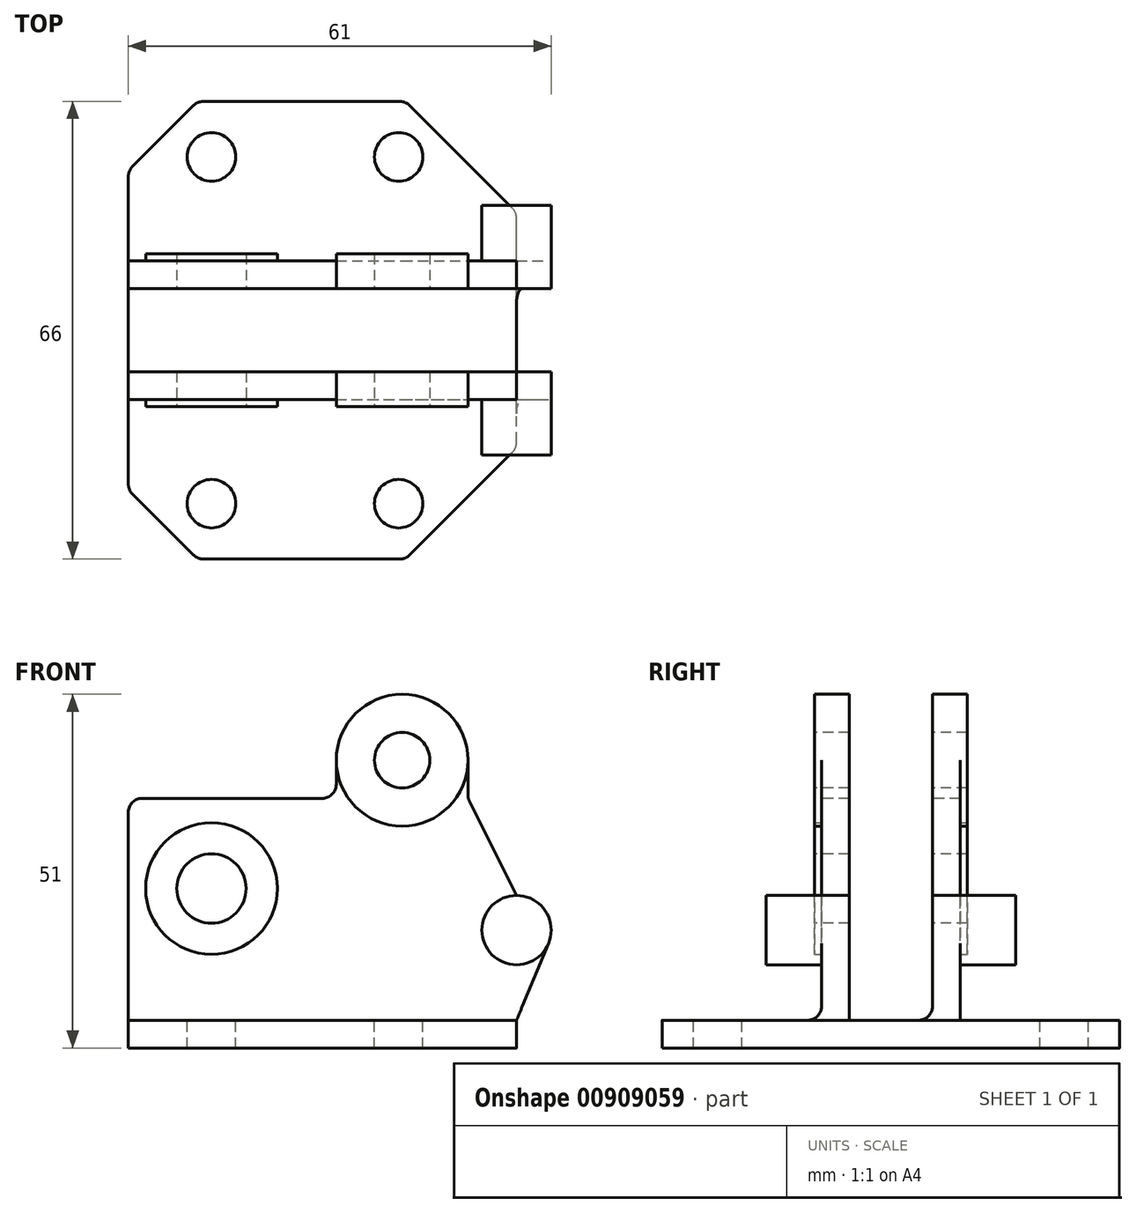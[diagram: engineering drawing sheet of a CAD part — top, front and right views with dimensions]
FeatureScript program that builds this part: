
annotation { "Feature Type Name" : "Feature", "Feature Type Description" : "" }
export const myFeature = defineFeature(function(context is Context, id is Id, definition is map)
    precondition{}
    {
        {
            var Q0;
            Q0=qCreatedBy(makeId("Top.planeOp"),FACE);
            var sketch = newSketch(context, id + "F0", { "sketchPlane" : qUnion([Q0])});
            skLineSegment(sketch, "E0.bottom", {"start": v(0, 0) * mm, "end": v(56, 0) * mm});
            skLineSegment(sketch, "E0.top", {"start": v(0, 66) * mm, "end": v(56, 66) * mm});
            skLineSegment(sketch, "E0.left", {"start": v(0, 0) * mm, "end": v(0, 66) * mm});
            skLineSegment(sketch, "E0.right", {"start": v(56, 0) * mm, "end": v(56, 66) * mm});
            skSolve(sketch);
        }
        {
            var Q0;
            Q0=makeQuery(id+"F0.imprint","IMPRINT",FACE,{"disambiguationData":[TD([[makeQuery(id+"F0.imprint","IMPRINT",EDGE,{"derivedFrom":sQuery(id+"F0.wireOp",EDGE,"E0.bottom")}),1.0]])]});
            extrude(context, id + "F1", {"entities" : qUnion([Q0]), "depth" : 4 * mm, "offsetDistance" : 25 * mm});
        }
        {
            var Q0;
            Q0=makeQuery(id+"F1.opExtrude","CAP_FACE",FACE,{"disambiguationData":[OSD([sQuery(id+"F0.wireOp",EDGE,"E0.bottom"),sQuery(id+"F0.wireOp",EDGE,"E0.top"),sQuery(id+"F0.wireOp",EDGE,"E0.left"),sQuery(id+"F0.wireOp",EDGE,"E0.right")])],"isStart":false});
            var sketch = newSketch(context, id + "F2", { "sketchPlane" : qUnion([Q0])});
            skPoint(sketch, "E1", {"position": v(12, 58) * mm});
            skPoint(sketch, "E2.0.1.0", {"position": v(12, 8) * mm});
            skPoint(sketch, "E2.1.0.0", {"position": v(39, 58) * mm});
            skPoint(sketch, "E2.1.1.0", {"position": v(39, 8) * mm});
            skLineSegment(sketch, "E2.direction1", {"start": v(12, 58) * mm, "end": v(39, 58) * mm, "construction": true});
            skLineSegment(sketch, "E2.direction2", {"start": v(12, 58) * mm, "end": v(12, 8) * mm, "construction": true});
            skSolve(sketch);
        }
        {
            var Q0;
            Q0=sQuery(id+"F2.wireOp",VERTEX,"E1");
            var Q1;
            Q1=sQuery(id+"F2.wireOp",VERTEX,"E2.1.0.0");
            var Q2;
            Q2=sQuery(id+"F2.wireOp",VERTEX,"E2.1.1.0");
            var Q3;
            Q3=sQuery(id+"F2.wireOp",VERTEX,"E2.0.1.0");
            var Q4;
            Q4=makeQuery(id+"F1.opExtrude","SWEPT_BODY",BODY,{"disambiguationData":[OSD([sQuery(id+"F0.wireOp",EDGE,"E0.bottom"),sQuery(id+"F0.wireOp",EDGE,"E0.top"),sQuery(id+"F0.wireOp",EDGE,"E0.left"),sQuery(id+"F0.wireOp",EDGE,"E0.right")])]});
            hole(context, id + "F3", {"style" : HoleStyle.SIMPLE, "endStyle" : HoleEndStyle.THROUGH, "holeDiameter" : 7 * mm, "majorDiameter" : 5 * mm, "isTappedThrough" : true, "tappedDepth" : 12 * mm, "tapClearance" : 3, "startFromSketch" : true, "locations" : qUnion([Q0, Q1, Q2, Q3]), "scope" : qUnion([Q4])});
        }
        {
            var Q0;
            Q0=makeQuery(id+"F1.opExtrude","SWEPT_EDGE",EDGE,{"disambiguationData":[OSD([sQuery(id+"F0.wireOp",EDGE,"E0.top"),sQuery(id+"F0.wireOp",EDGE,"E0.left")])]});
            var Q1;
            Q1=makeQuery(id+"F1.opExtrude","SWEPT_EDGE",EDGE,{"disambiguationData":[OSD([sQuery(id+"F0.wireOp",EDGE,"E0.bottom"),sQuery(id+"F0.wireOp",EDGE,"E0.left")])]});
            chamfer(context, id + "F4", {"entities" : qUnion([Q0, Q1]), "chamferType" : ChamferType.OFFSET_ANGLE, "width" : 10 * mm, "oppositeDirection" : false, "angle" : 45 * degree, "tangentPropagation" : true});
        }
        {
            var Q0;
            Q0=makeQuery(id+"F1.opExtrude","SWEPT_EDGE",EDGE,{"disambiguationData":[OSD([sQuery(id+"F0.wireOp",EDGE,"E0.top"),sQuery(id+"F0.wireOp",EDGE,"E0.right")])]});
            var Q1;
            Q1=makeQuery(id+"F1.opExtrude","SWEPT_EDGE",EDGE,{"disambiguationData":[OSD([sQuery(id+"F0.wireOp",EDGE,"E0.bottom"),sQuery(id+"F0.wireOp",EDGE,"E0.right")])]});
            chamfer(context, id + "F5", {"entities" : qUnion([Q0, Q1]), "chamferType" : ChamferType.OFFSET_ANGLE, "width" : 16 * mm, "oppositeDirection" : false, "angle" : 45 * degree, "tangentPropagation" : true});
        }
        {
            var Q0;
            Q0=makeQuery(id+"F1.opExtrude","SWEPT_FACE",FACE,{"disambiguationData":[OSD([sQuery(id+"F0.wireOp",EDGE,"E0.bottom")])]});
            var Q1;
            Q1=makeQuery(id+"F1.opExtrude","SWEPT_FACE",FACE,{"disambiguationData":[OSD([sQuery(id+"F0.wireOp",EDGE,"E0.top")])]});
            cPlane(context, id + "F6", {"entities" : qUnion([Q0, Q1]), "cplaneType" : CPlaneType.MID_PLANE, "offset" : 25 * mm, "width" : 150 * mm, "height" : 150 * mm});
        }
        {
            var Q0;
            Q0=qCreatedBy(id+"F6.planeOp",FACE);
            var sketch = newSketch(context, id + "F7", { "sketchPlane" : qUnion([Q0])});
            skPoint(sketch, "E3.0", {"position": v(0, 4) * mm});
            skPoint(sketch, "E4.0", {"position": v(56, 4) * mm});
            skLineSegment(sketch, "E5", {"start": v(0, 4) * mm, "end": v(0, 36) * mm});
            skLineSegment(sketch, "E6", {"start": v(0, 36) * mm, "end": v(30, 36) * mm});
            skLineSegment(sketch, "E7", {"start": v(0, 4) * mm, "end": v(56, 4) * mm});
            skArc(sketch, "E8", {"start": v(49, 41.5) * mm, "mid": v(39.5, 51) * mm, "end": v(30, 41.5) * mm});
            skArc(sketch, "E9", {"start": v(60.62, 15.08) * mm, "mid": v(60.16, 19.77) * mm, "end": v(56, 22) * mm});
            skLineSegment(sketch, "E10", {"start": v(56, 4) * mm, "end": v(60.62, 15.08) * mm});
            skLineSegment(sketch, "E11", {"start": v(56, 17) * mm, "end": v(56, 70.27) * mm, "construction": true});
            skLineSegment(sketch, "E12", {"start": v(49, 36) * mm, "end": v(56, 22) * mm});
            skLineSegment(sketch, "E13", {"start": v(30, 41.5) * mm, "end": v(30, 36) * mm});
            skLineSegment(sketch, "E14", {"start": v(49, 41.5) * mm, "end": v(49, 36) * mm});
            skSolve(sketch);
        }
        {
            var Q0;
            Q0 = qSketchRegion(id + "F7", true);
            extrude(context, id + "F8", {"entities" : qUnion([Q0]), "oppositeDirection" : true, "depth" : 10 * mm, "offsetDistance" : 25 * mm, "hasSecondDirection" : true, "secondDirectionOppositeDirection" : false, "secondDirectionDepth" : 10 * mm});
        }
        {
            var Q0;
            Q0=makeQuery(id+"F8.opExtrude","SWEPT_EDGE",EDGE,{"disambiguationData":[OSD([sQuery(id+"F7.wireOp",EDGE,"E6"),sQuery(id+"F7.wireOp",EDGE,"E13")])]});
            var Q1;
            Q1=makeQuery(id+"F8.opExtrude","SWEPT_EDGE",EDGE,{"disambiguationData":[OSD([sQuery(id+"F7.wireOp",EDGE,"E12"),sQuery(id+"F7.wireOp",EDGE,"E14")])]});
            var Q2;
            Q2=makeQuery(id+"F8.opExtrude","SWEPT_EDGE",EDGE,{"disambiguationData":[OSD([sQuery(id+"F7.wireOp",EDGE,"E5"),sQuery(id+"F7.wireOp",EDGE,"E6")])]});
            fillet(context, id + "F9", {"entities" : qUnion([Q0, Q1, Q2]), "radius" : 2 * mm, "tangentPropagation" : true, "allowEdgeOverflow" : false});
        }
        {
            var Q0;
            Q0=makeQuery(id+"F8.opExtrude","SWEPT_FACE",FACE,{"disambiguationData":[OSD([sQuery(id+"F7.wireOp",EDGE,"E5")])]});
            var sketch = newSketch(context, id + "F10", { "sketchPlane" : qUnion([Q0])});
            skLineSegment(sketch, "E15.bottom", {"start": v(-39, 4) * mm, "end": v(-27, 4) * mm});
            skLineSegment(sketch, "E15.top", {"start": v(-39, 54) * mm, "end": v(-27, 54) * mm});
            skLineSegment(sketch, "E15.left", {"start": v(-39, 4) * mm, "end": v(-39, 54) * mm});
            skLineSegment(sketch, "E15.right", {"start": v(-27, 4) * mm, "end": v(-27, 54) * mm});
            skSolve(sketch);
        }
        {
            var Q0;
            Q0=makeQuery(id+"F8.opExtrude","CAP_FACE",FACE,{"disambiguationData":[OSD([sQuery(id+"F7.wireOp",EDGE,"E5"),sQuery(id+"F7.wireOp",EDGE,"E6"),sQuery(id+"F7.wireOp",EDGE,"E7"),sQuery(id+"F7.wireOp",EDGE,"E8"),sQuery(id+"F7.wireOp",EDGE,"E9"),sQuery(id+"F7.wireOp",EDGE,"E10"),sQuery(id+"F7.wireOp",EDGE,"E12"),sQuery(id+"F7.wireOp",EDGE,"E13"),sQuery(id+"F7.wireOp",EDGE,"E14")])],"isStart":true});
            var sketch = newSketch(context, id + "F11", { "sketchPlane" : qUnion([Q0])});
            skCircle(sketch, "E16", {"center": v(12, 23) * mm, "radius": 9.5 * mm});
            skCircle(sketch, "E17", {"center": v(12, 23) * mm, "radius": 5 * mm});
            skCircle(sketch, "E18", {"center": v(39.5, 41.5) * mm, "radius": 9.5 * mm});
            skCircle(sketch, "E19", {"center": v(56, 17) * mm, "radius": 5 * mm});
            skCircle(sketch, "E20", {"center": v(39.5, 41.5) * mm, "radius": 4 * mm});
            skSolve(sketch);
        }
        {
            var Q0;
            Q0=makeQuery(id+"F11.imprint","IMPRINT",FACE,{"disambiguationData":[TD([[makeQuery(id+"F11.imprint","IMPRINT",EDGE,{"derivedFrom":sQuery(id+"F11.wireOp",EDGE,"E17")}),1.0]])]});
            var Q1;
            Q1=makeQuery(id+"F11.imprint","IMPRINT",FACE,{"disambiguationData":[TD([[makeQuery(id+"F11.imprint","IMPRINT",EDGE,{"derivedFrom":sQuery(id+"F11.wireOp",EDGE,"E20")}),1.0]])]});
            extrude(context, id + "F12", {"entities" : qUnion([Q0, Q1]), "operationType" : NewBodyOperationType.REMOVE, "endBound" : BoundingType.UP_TO_NEXT, "oppositeDirection" : true, "depth" : 25 * mm, "offsetDistance" : 25 * mm});
        }
        {
            var Q0;
            Q0=makeQuery(id+"F11.imprint","IMPRINT",FACE,{"disambiguationData":[TD([[makeQuery(id+"F11.imprint","IMPRINT",EDGE,{"derivedFrom":sQuery(id+"F11.wireOp",EDGE,"E16")}),1.0]])]});
            var Q1;
            Q1=makeQuery(id+"F11.imprint","IMPRINT",FACE,{"disambiguationData":[TD([[makeQuery(id+"F11.imprint","IMPRINT",EDGE,{"derivedFrom":sQuery(id+"F11.wireOp",EDGE,"E20")}),-1.0]])]});
            extrude(context, id + "F13", {"entities" : qUnion([Q0, Q1]), "operationType" : NewBodyOperationType.ADD, "depth" : 1 * mm, "offsetDistance" : 25 * mm, "hasSecondDirection" : true, "secondDirectionOppositeDirection" : true, "secondDirectionDepth" : 21 * mm});
        }
        {
            var Q0;
            Q0=makeQuery(id+"F8.opExtrude","CAP_FACE",FACE,{"disambiguationData":[OSD([sQuery(id+"F7.wireOp",EDGE,"E5"),sQuery(id+"F7.wireOp",EDGE,"E6"),sQuery(id+"F7.wireOp",EDGE,"E7"),sQuery(id+"F7.wireOp",EDGE,"E8"),sQuery(id+"F7.wireOp",EDGE,"E9"),sQuery(id+"F7.wireOp",EDGE,"E10"),sQuery(id+"F7.wireOp",EDGE,"E12"),sQuery(id+"F7.wireOp",EDGE,"E13"),sQuery(id+"F7.wireOp",EDGE,"E14")])],"isStart":true});
            var sketch = newSketch(context, id + "F14", { "sketchPlane" : qUnion([Q0])});
            skCircle(sketch, "E21", {"center": v(56, 17) * mm, "radius": 5 * mm});
            skSolve(sketch);
        }
        {
            var Q0;
            {var subQ0=sQuery(id+"F14.wireOp",EDGE,"E21");var subQ1=makeQuery(id+"F14.imprint","INTERSECT",VERTEX,{"derivedFrom":[makeQuery(id+"F8.opExtrude","CAP_EDGE",EDGE,{"disambiguationData":[OSD([sQuery(id+"F7.wireOp",EDGE,"E10")])],"isStart":true}),subQ0]});Q0=makeQuery(id+"F14.imprint","IMPRINT",FACE,{"disambiguationData":[TD([[makeQuery(id+"F14.imprint","IMPRINT",EDGE,{"disambiguationData":[TD([[subQ1,-1.0]])],"derivedFrom":subQ0}),1.0]])]});}
            extrude(context, id + "F15", {"entities" : qUnion([Q0]), "operationType" : NewBodyOperationType.ADD, "depth" : 8 * mm, "offsetDistance" : 25 * mm, "hasSecondDirection" : true, "secondDirectionOppositeDirection" : true, "secondDirectionDepth" : 28 * mm});
        }
        {
            var Q0;
            Q0 = qSketchRegion(id + "F10", true);
            extrude(context, id + "F16", {"entities" : qUnion([Q0]), "operationType" : NewBodyOperationType.REMOVE, "endBound" : BoundingType.THROUGH_ALL, "oppositeDirection" : true, "depth" : 25 * mm, "offsetDistance" : 25 * mm});
        }
        {
            var Q0;
            Q0=makeQuery(id+"F1.opExtrude","SWEPT_BODY",BODY,{"disambiguationData":[OSD([sQuery(id+"F0.wireOp",EDGE,"E0.bottom"),sQuery(id+"F0.wireOp",EDGE,"E0.top"),sQuery(id+"F0.wireOp",EDGE,"E0.left"),sQuery(id+"F0.wireOp",EDGE,"E0.right")])]});
            var Q1;
            Q1=makeQuery(id+"F16.boolean.opBoolean","SPLIT",BODY,{"disambiguationData":[OD(0.0)],"derivedFrom":makeQuery(id+"F8.opExtrude","SWEPT_BODY",BODY,{"disambiguationData":[OSD([sQuery(id+"F7.wireOp",EDGE,"E5"),sQuery(id+"F7.wireOp",EDGE,"E6"),sQuery(id+"F7.wireOp",EDGE,"E7"),sQuery(id+"F7.wireOp",EDGE,"E8"),sQuery(id+"F7.wireOp",EDGE,"E9"),sQuery(id+"F7.wireOp",EDGE,"E10"),sQuery(id+"F7.wireOp",EDGE,"E12"),sQuery(id+"F7.wireOp",EDGE,"E13"),sQuery(id+"F7.wireOp",EDGE,"E14")])]})});
            var Q2;
            Q2=makeQuery(id+"F16.boolean.opBoolean","SPLIT",BODY,{"disambiguationData":[OD(1.0)],"derivedFrom":makeQuery(id+"F8.opExtrude","SWEPT_BODY",BODY,{"disambiguationData":[OSD([sQuery(id+"F7.wireOp",EDGE,"E5"),sQuery(id+"F7.wireOp",EDGE,"E6"),sQuery(id+"F7.wireOp",EDGE,"E7"),sQuery(id+"F7.wireOp",EDGE,"E8"),sQuery(id+"F7.wireOp",EDGE,"E9"),sQuery(id+"F7.wireOp",EDGE,"E10"),sQuery(id+"F7.wireOp",EDGE,"E12"),sQuery(id+"F7.wireOp",EDGE,"E13"),sQuery(id+"F7.wireOp",EDGE,"E14")])]})});
            booleanBodies(context, id + "F17", {"operationType" : BooleanOperationType.UNION, "tools" : qUnion([Q0, Q1, Q2])});
        }
        {
            var Q0;
            Q0=makeQuery(id+"F8.opExtrude","CAP_EDGE",EDGE,{"disambiguationData":[OSD([sQuery(id+"F7.wireOp",EDGE,"E7")])],"isStart":true});
            var Q1;
            Q1=makeQuery(id+"F16.boolean.opBoolean","COPY",EDGE,{"derivedFrom":makeQuery(id+"F16.opExtrude","SWEPT_EDGE",EDGE,{"disambiguationData":[OSD([sQuery(id+"F7.wireOp",EDGE,"E5"),sQuery(id+"F7.wireOp",EDGE,"E7"),sQuery(id+"F10.wireOp",EDGE,"E15.bottom"),sQuery(id+"F10.wireOp",EDGE,"E15.left")])]})});
            var Q2;
            Q2=makeQuery(id+"F8.opExtrude","CAP_EDGE",EDGE,{"disambiguationData":[OSD([sQuery(id+"F7.wireOp",EDGE,"E7")])],"isStart":false});
            var Q3;
            Q3=makeQuery(id+"F16.boolean.opBoolean","COPY",EDGE,{"derivedFrom":makeQuery(id+"F16.opExtrude","SWEPT_EDGE",EDGE,{"disambiguationData":[OSD([sQuery(id+"F7.wireOp",EDGE,"E5"),sQuery(id+"F7.wireOp",EDGE,"E7"),sQuery(id+"F10.wireOp",EDGE,"E15.bottom"),sQuery(id+"F10.wireOp",EDGE,"E15.right")])]})});
            fillet(context, id + "F18", {"entities" : qUnion([Q0, Q1, Q2, Q3]), "radius" : 2 * mm, "tangentPropagation" : true, "allowEdgeOverflow" : false});
        }
        {
            var Q0;
            {var subQ0=sQuery(id+"F0.wireOp",EDGE,"E0.bottom");Q0=makeQuery(id+"F5.opChamfer","BLEND_EDGE",EDGE,{"blendedFrom":[makeQuery(id+"F1.opExtrude","SWEPT_EDGE",EDGE,{"disambiguationData":[OSD([subQ0,sQuery(id+"F0.wireOp",EDGE,"E0.right")])]}),makeQuery(id+"F1.opExtrude","SWEPT_FACE",FACE,{"disambiguationData":[OSD([subQ0])]})],"blendedInto":[makeQuery(id+"F1.opExtrude","SWEPT_FACE",FACE,{"disambiguationData":[OSD([subQ0])]})]});}
            var Q1;
            {var subQ0=sQuery(id+"F0.wireOp",EDGE,"E0.right");Q1=makeQuery(id+"F5.opChamfer","BLEND_EDGE",EDGE,{"blendedFrom":[makeQuery(id+"F1.opExtrude","SWEPT_EDGE",EDGE,{"disambiguationData":[OSD([sQuery(id+"F0.wireOp",EDGE,"E0.bottom"),subQ0])]}),makeQuery(id+"F1.opExtrude","SWEPT_FACE",FACE,{"disambiguationData":[OSD([subQ0])]})],"blendedInto":[makeQuery(id+"F1.opExtrude","SWEPT_FACE",FACE,{"disambiguationData":[OSD([subQ0])]})]});}
            var Q2;
            {var subQ0=sQuery(id+"F0.wireOp",EDGE,"E0.bottom");Q2=makeQuery(id+"F4.opChamfer","BLEND_EDGE",EDGE,{"blendedFrom":[makeQuery(id+"F1.opExtrude","SWEPT_EDGE",EDGE,{"disambiguationData":[OSD([subQ0,sQuery(id+"F0.wireOp",EDGE,"E0.left")])]}),makeQuery(id+"F1.opExtrude","SWEPT_FACE",FACE,{"disambiguationData":[OSD([subQ0])]})],"blendedInto":[makeQuery(id+"F1.opExtrude","SWEPT_FACE",FACE,{"disambiguationData":[OSD([subQ0])]})]});}
            var Q3;
            {var subQ0=sQuery(id+"F0.wireOp",EDGE,"E0.right");Q3=makeQuery(id+"F5.opChamfer","BLEND_EDGE",EDGE,{"blendedFrom":[makeQuery(id+"F1.opExtrude","SWEPT_EDGE",EDGE,{"disambiguationData":[OSD([sQuery(id+"F0.wireOp",EDGE,"E0.top"),subQ0])]}),makeQuery(id+"F1.opExtrude","SWEPT_FACE",FACE,{"disambiguationData":[OSD([subQ0])]})],"blendedInto":[makeQuery(id+"F1.opExtrude","SWEPT_FACE",FACE,{"disambiguationData":[OSD([subQ0])]})]});}
            var Q4;
            {var subQ0=sQuery(id+"F0.wireOp",EDGE,"E0.top");Q4=makeQuery(id+"F5.opChamfer","BLEND_EDGE",EDGE,{"blendedFrom":[makeQuery(id+"F1.opExtrude","SWEPT_EDGE",EDGE,{"disambiguationData":[OSD([subQ0,sQuery(id+"F0.wireOp",EDGE,"E0.right")])]}),makeQuery(id+"F1.opExtrude","SWEPT_FACE",FACE,{"disambiguationData":[OSD([subQ0])]})],"blendedInto":[makeQuery(id+"F1.opExtrude","SWEPT_FACE",FACE,{"disambiguationData":[OSD([subQ0])]})]});}
            var Q5;
            {var subQ0=sQuery(id+"F0.wireOp",EDGE,"E0.top");Q5=makeQuery(id+"F4.opChamfer","BLEND_EDGE",EDGE,{"blendedFrom":[makeQuery(id+"F1.opExtrude","SWEPT_EDGE",EDGE,{"disambiguationData":[OSD([subQ0,sQuery(id+"F0.wireOp",EDGE,"E0.left")])]}),makeQuery(id+"F1.opExtrude","SWEPT_FACE",FACE,{"disambiguationData":[OSD([subQ0])]})],"blendedInto":[makeQuery(id+"F1.opExtrude","SWEPT_FACE",FACE,{"disambiguationData":[OSD([subQ0])]})]});}
            var Q6;
            {var subQ0=sQuery(id+"F0.wireOp",EDGE,"E0.left");Q6=makeQuery(id+"F4.opChamfer","BLEND_EDGE",EDGE,{"blendedFrom":[makeQuery(id+"F1.opExtrude","SWEPT_EDGE",EDGE,{"disambiguationData":[OSD([sQuery(id+"F0.wireOp",EDGE,"E0.top"),subQ0])]}),makeQuery(id+"F1.opExtrude","SWEPT_FACE",FACE,{"disambiguationData":[OSD([subQ0])]})],"blendedInto":[makeQuery(id+"F1.opExtrude","SWEPT_FACE",FACE,{"disambiguationData":[OSD([subQ0])]})]});}
            var Q7;
            {var subQ0=sQuery(id+"F0.wireOp",EDGE,"E0.left");Q7=makeQuery(id+"F4.opChamfer","BLEND_EDGE",EDGE,{"blendedFrom":[makeQuery(id+"F1.opExtrude","SWEPT_EDGE",EDGE,{"disambiguationData":[OSD([sQuery(id+"F0.wireOp",EDGE,"E0.bottom"),subQ0])]}),makeQuery(id+"F1.opExtrude","SWEPT_FACE",FACE,{"disambiguationData":[OSD([subQ0])]})],"blendedInto":[makeQuery(id+"F1.opExtrude","SWEPT_FACE",FACE,{"disambiguationData":[OSD([subQ0])]})]});}
            fillet(context, id + "F19", {"entities" : qUnion([Q0, Q1, Q2, Q3, Q4, Q5, Q6, Q7]), "radius" : 2 * mm, "tangentPropagation" : true, "allowEdgeOverflow" : false});
        }
    });
